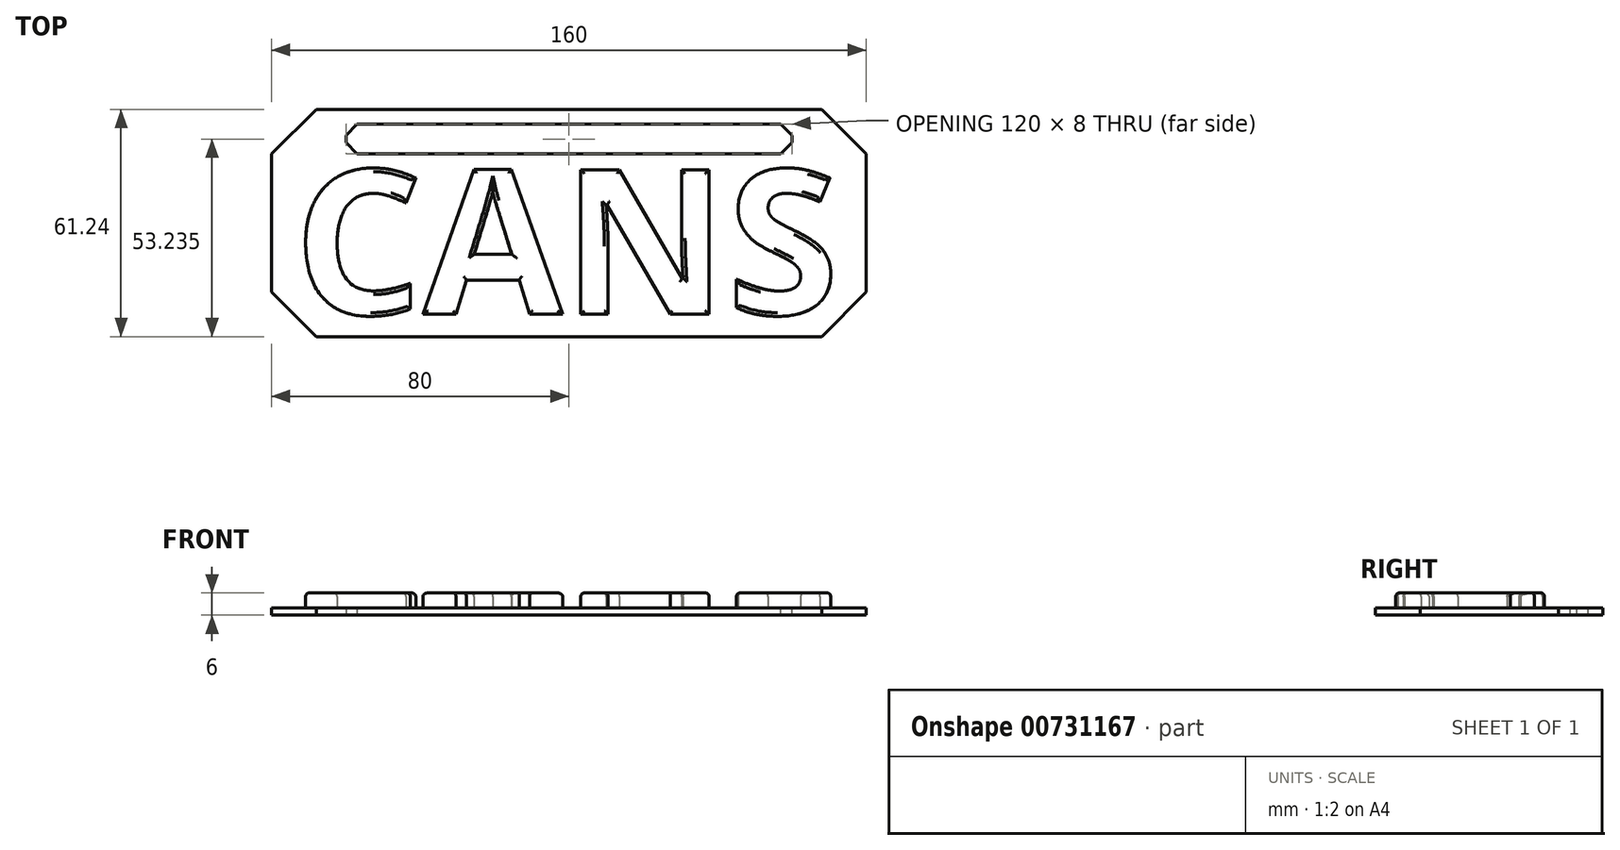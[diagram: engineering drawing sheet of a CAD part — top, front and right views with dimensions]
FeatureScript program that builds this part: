
annotation { "Feature Type Name" : "Feature", "Feature Type Description" : "" }
export const myFeature = defineFeature(function(context is Context, id is Id, definition is map)
    precondition{}
    {
        {
            var Q0;
            Q0=qCreatedBy(makeId("Top.planeOp"),FACE);
            var sketch = newSketch(context, id + "F0", { "sketchPlane" : qUnion([Q0])});
            skLineSegment(sketch, "E0.bottom", {"start": v(-80, 30.62) * mm, "end": v(80, 30.62) * mm});
            skLineSegment(sketch, "E0.top", {"start": v(-80, -30.62) * mm, "end": v(80, -30.62) * mm});
            skLineSegment(sketch, "E0.left", {"start": v(-80, 30.62) * mm, "end": v(-80, -30.62) * mm});
            skLineSegment(sketch, "E0.right", {"start": v(80, 30.62) * mm, "end": v(80, -30.62) * mm});
            skLineSegment(sketch, "E1", {"start": v(-80, 30.62) * mm, "end": v(80, -30.62) * mm, "construction": true});
            skText(sketch, "E2", { "text": "CANS", "fontName": "OpenSans-Bold.ttf"});
            skLineSegment(sketch, "E3", {"start": v(-74, -24.62) * mm, "end": v(-74, -30.62) * mm, "construction": true});
            skLineSegment(sketch, "E4", {"start": v(-74, 14.62) * mm, "end": v(-80, 14.62) * mm, "construction": true});
            skLineSegment(sketch, "E5", {"start": v(74, 14.62) * mm, "end": v(80, 14.62) * mm, "construction": true});
            skLineSegment(sketch, "E6.bottom", {"start": v(-60, 26.62) * mm, "end": v(60, 26.62) * mm});
            skLineSegment(sketch, "E6.top", {"start": v(-60, 18.62) * mm, "end": v(60, 18.62) * mm});
            skLineSegment(sketch, "E6.left", {"start": v(-60, 26.62) * mm, "end": v(-60, 18.62) * mm});
            skLineSegment(sketch, "E6.right", {"start": v(60, 26.62) * mm, "end": v(60, 18.62) * mm});
            skLineSegment(sketch, "E7", {"start": v(-60, 26.62) * mm, "end": v(-80, 26.62) * mm, "construction": true});
            skLineSegment(sketch, "E8", {"start": v(60, 26.62) * mm, "end": v(80, 26.62) * mm, "construction": true});
            const initialGuessF0  = {"E2": [-0.074, -0.02462, 1, 0, 0.03923]};
            skSetInitialGuess(sketch, initialGuessF0);
            skSolve(sketch);
        }
        {
            var Q0;
            Q0=makeQuery(id+"F0.imprint","IMPRINT",FACE,{"disambiguationData":[TD([[makeQuery(id+"F0.imprint","IMPRINT",EDGE,{"derivedFrom":sQuery(id+"F0.wireOp",EDGE,"E0.bottom")}),-1.0]])]});
            var Q1;
            Q1=makeQuery(id+"F0.imprint","IMPRINT",FACE,{"disambiguationData":[TD([[makeQuery(id+"F0.imprint","IMPRINT",EDGE,{"derivedFrom":sQuery(id+"F0.wireOp",EDGE,"E2.sketch_text.stroke-23")}),1.0]])]});
            extrude(context, id + "F1", {"entities" : qUnion([Q0, Q1]), "depth" : 2 * mm, "offsetDistance" : 25 * mm});
        }
        {
            var Q0;
            Q0=makeQuery(id+"F0.imprint","IMPRINT",FACE,{"disambiguationData":[TD([[makeQuery(id+"F0.imprint","IMPRINT",EDGE,{"derivedFrom":sQuery(id+"F0.wireOp",EDGE,"E2.sketch_text.stroke-0")}),-1.0]])]});
            var Q1;
            Q1=makeQuery(id+"F0.imprint","IMPRINT",FACE,{"disambiguationData":[TD([[makeQuery(id+"F0.imprint","IMPRINT",EDGE,{"derivedFrom":sQuery(id+"F0.wireOp",EDGE,"E2.sketch_text.stroke-15")}),-1.0]])]});
            var Q2;
            Q2=makeQuery(id+"F0.imprint","IMPRINT",FACE,{"disambiguationData":[TD([[makeQuery(id+"F0.imprint","IMPRINT",EDGE,{"derivedFrom":sQuery(id+"F0.wireOp",EDGE,"E2.sketch_text.stroke-27")}),-1.0]])]});
            var Q3;
            Q3=makeQuery(id+"F0.imprint","IMPRINT",FACE,{"disambiguationData":[TD([[makeQuery(id+"F0.imprint","IMPRINT",EDGE,{"derivedFrom":sQuery(id+"F0.wireOp",EDGE,"E2.sketch_text.stroke-41")}),-1.0]])]});
            extrude(context, id + "F2", {"entities" : qUnion([Q0, Q1, Q2, Q3]), "operationType" : NewBodyOperationType.ADD, "depth" : 6 * mm, "offsetDistance" : 25 * mm});
        }
        {
            var Q0;
            Q0=makeQuery(id+"F2.opExtrude","CAP_FACE",FACE,{"disambiguationData":[OSD([sQuery(id+"F0.wireOp",EDGE,"E2.sketch_text.stroke-0"),sQuery(id+"F0.wireOp",EDGE,"E2.sketch_text.stroke-1"),sQuery(id+"F0.wireOp",EDGE,"E2.sketch_text.stroke-2"),sQuery(id+"F0.wireOp",EDGE,"E2.sketch_text.stroke-3"),sQuery(id+"F0.wireOp",EDGE,"E2.sketch_text.stroke-4"),sQuery(id+"F0.wireOp",EDGE,"E2.sketch_text.stroke-5"),sQuery(id+"F0.wireOp",EDGE,"E2.sketch_text.stroke-6"),sQuery(id+"F0.wireOp",EDGE,"E2.sketch_text.stroke-7"),sQuery(id+"F0.wireOp",EDGE,"E2.sketch_text.stroke-8"),sQuery(id+"F0.wireOp",EDGE,"E2.sketch_text.stroke-9"),sQuery(id+"F0.wireOp",EDGE,"E2.sketch_text.stroke-10"),sQuery(id+"F0.wireOp",EDGE,"E2.sketch_text.stroke-11"),sQuery(id+"F0.wireOp",EDGE,"E2.sketch_text.stroke-12"),sQuery(id+"F0.wireOp",EDGE,"E2.sketch_text.stroke-13"),sQuery(id+"F0.wireOp",EDGE,"E2.sketch_text.stroke-14")])],"isStart":false});
            var Q1;
            Q1=makeQuery(id+"F2.opExtrude","CAP_FACE",FACE,{"disambiguationData":[OSD([sQuery(id+"F0.wireOp",EDGE,"E2.sketch_text.stroke-15"),sQuery(id+"F0.wireOp",EDGE,"E2.sketch_text.stroke-16"),sQuery(id+"F0.wireOp",EDGE,"E2.sketch_text.stroke-17"),sQuery(id+"F0.wireOp",EDGE,"E2.sketch_text.stroke-18"),sQuery(id+"F0.wireOp",EDGE,"E2.sketch_text.stroke-19"),sQuery(id+"F0.wireOp",EDGE,"E2.sketch_text.stroke-20"),sQuery(id+"F0.wireOp",EDGE,"E2.sketch_text.stroke-21"),sQuery(id+"F0.wireOp",EDGE,"E2.sketch_text.stroke-22"),sQuery(id+"F0.wireOp",EDGE,"E2.sketch_text.stroke-23"),sQuery(id+"F0.wireOp",EDGE,"E2.sketch_text.stroke-24"),sQuery(id+"F0.wireOp",EDGE,"E2.sketch_text.stroke-25"),sQuery(id+"F0.wireOp",EDGE,"E2.sketch_text.stroke-26")])],"isStart":false});
            var Q2;
            Q2=makeQuery(id+"F2.opExtrude","CAP_FACE",FACE,{"disambiguationData":[OSD([sQuery(id+"F0.wireOp",EDGE,"E2.sketch_text.stroke-27"),sQuery(id+"F0.wireOp",EDGE,"E2.sketch_text.stroke-28"),sQuery(id+"F0.wireOp",EDGE,"E2.sketch_text.stroke-29"),sQuery(id+"F0.wireOp",EDGE,"E2.sketch_text.stroke-30"),sQuery(id+"F0.wireOp",EDGE,"E2.sketch_text.stroke-31"),sQuery(id+"F0.wireOp",EDGE,"E2.sketch_text.stroke-32"),sQuery(id+"F0.wireOp",EDGE,"E2.sketch_text.stroke-33"),sQuery(id+"F0.wireOp",EDGE,"E2.sketch_text.stroke-34"),sQuery(id+"F0.wireOp",EDGE,"E2.sketch_text.stroke-35"),sQuery(id+"F0.wireOp",EDGE,"E2.sketch_text.stroke-36"),sQuery(id+"F0.wireOp",EDGE,"E2.sketch_text.stroke-37"),sQuery(id+"F0.wireOp",EDGE,"E2.sketch_text.stroke-38"),sQuery(id+"F0.wireOp",EDGE,"E2.sketch_text.stroke-39"),sQuery(id+"F0.wireOp",EDGE,"E2.sketch_text.stroke-40")])],"isStart":false});
            var Q3;
            Q3=makeQuery(id+"F2.opExtrude","CAP_FACE",FACE,{"disambiguationData":[OSD([sQuery(id+"F0.wireOp",EDGE,"E2.sketch_text.stroke-41"),sQuery(id+"F0.wireOp",EDGE,"E2.sketch_text.stroke-42"),sQuery(id+"F0.wireOp",EDGE,"E2.sketch_text.stroke-43"),sQuery(id+"F0.wireOp",EDGE,"E2.sketch_text.stroke-44"),sQuery(id+"F0.wireOp",EDGE,"E2.sketch_text.stroke-45"),sQuery(id+"F0.wireOp",EDGE,"E2.sketch_text.stroke-46"),sQuery(id+"F0.wireOp",EDGE,"E2.sketch_text.stroke-47"),sQuery(id+"F0.wireOp",EDGE,"E2.sketch_text.stroke-48"),sQuery(id+"F0.wireOp",EDGE,"E2.sketch_text.stroke-49"),sQuery(id+"F0.wireOp",EDGE,"E2.sketch_text.stroke-50"),sQuery(id+"F0.wireOp",EDGE,"E2.sketch_text.stroke-51"),sQuery(id+"F0.wireOp",EDGE,"E2.sketch_text.stroke-52"),sQuery(id+"F0.wireOp",EDGE,"E2.sketch_text.stroke-53"),sQuery(id+"F0.wireOp",EDGE,"E2.sketch_text.stroke-54"),sQuery(id+"F0.wireOp",EDGE,"E2.sketch_text.stroke-55"),sQuery(id+"F0.wireOp",EDGE,"E2.sketch_text.stroke-56"),sQuery(id+"F0.wireOp",EDGE,"E2.sketch_text.stroke-57"),sQuery(id+"F0.wireOp",EDGE,"E2.sketch_text.stroke-58"),sQuery(id+"F0.wireOp",EDGE,"E2.sketch_text.stroke-59"),sQuery(id+"F0.wireOp",EDGE,"E2.sketch_text.stroke-60"),sQuery(id+"F0.wireOp",EDGE,"E2.sketch_text.stroke-61"),sQuery(id+"F0.wireOp",EDGE,"E2.sketch_text.stroke-62"),sQuery(id+"F0.wireOp",EDGE,"E2.sketch_text.stroke-63"),sQuery(id+"F0.wireOp",EDGE,"E2.sketch_text.stroke-64"),sQuery(id+"F0.wireOp",EDGE,"E2.sketch_text.stroke-65"),sQuery(id+"F0.wireOp",EDGE,"E2.sketch_text.stroke-66"),sQuery(id+"F0.wireOp",EDGE,"E2.sketch_text.stroke-67"),sQuery(id+"F0.wireOp",EDGE,"E2.sketch_text.stroke-68")])],"isStart":false});
            fillet(context, id + "F3", {"entities" : qUnion([Q0, Q1, Q2, Q3]), "radius" : 1 * mm, "tangentPropagation" : true, "allowEdgeOverflow" : false});
        }
        {
            var Q0;
            Q0=makeQuery(id+"F1.opExtrude","SWEPT_EDGE",EDGE,{"disambiguationData":[OSD([sQuery(id+"F0.wireOp",EDGE,"E0.top"),sQuery(id+"F0.wireOp",EDGE,"E0.left")])]});
            var Q1;
            Q1=makeQuery(id+"F1.opExtrude","SWEPT_EDGE",EDGE,{"disambiguationData":[OSD([sQuery(id+"F0.wireOp",EDGE,"E0.bottom"),sQuery(id+"F0.wireOp",EDGE,"E0.left")])]});
            var Q2;
            Q2=makeQuery(id+"F1.opExtrude","SWEPT_EDGE",EDGE,{"disambiguationData":[OSD([sQuery(id+"F0.wireOp",EDGE,"E0.bottom"),sQuery(id+"F0.wireOp",EDGE,"E0.right")])]});
            var Q3;
            Q3=makeQuery(id+"F1.opExtrude","SWEPT_EDGE",EDGE,{"disambiguationData":[OSD([sQuery(id+"F0.wireOp",EDGE,"E0.top"),sQuery(id+"F0.wireOp",EDGE,"E0.right")])]});
            chamfer(context, id + "F4", {"entities" : qUnion([Q0, Q1, Q2, Q3]), "width" : 12 * mm, "tangentPropagation" : true});
        }
        {
            var Q0;
            Q0=makeQuery(id+"F1.opExtrude","SWEPT_EDGE",EDGE,{"disambiguationData":[OSD([sQuery(id+"F0.wireOp",EDGE,"E6.top"),sQuery(id+"F0.wireOp",EDGE,"E6.left")])]});
            var Q1;
            Q1=makeQuery(id+"F1.opExtrude","SWEPT_EDGE",EDGE,{"disambiguationData":[OSD([sQuery(id+"F0.wireOp",EDGE,"E6.bottom"),sQuery(id+"F0.wireOp",EDGE,"E6.left")])]});
            var Q2;
            Q2=makeQuery(id+"F1.opExtrude","SWEPT_EDGE",EDGE,{"disambiguationData":[OSD([sQuery(id+"F0.wireOp",EDGE,"E6.top"),sQuery(id+"F0.wireOp",EDGE,"E6.right")])]});
            var Q3;
            Q3=makeQuery(id+"F1.opExtrude","SWEPT_EDGE",EDGE,{"disambiguationData":[OSD([sQuery(id+"F0.wireOp",EDGE,"E6.bottom"),sQuery(id+"F0.wireOp",EDGE,"E6.right")])]});
            chamfer(context, id + "F5", {"entities" : qUnion([Q0, Q1, Q2, Q3]), "width" : 3 * mm, "tangentPropagation" : true});
        }
    });
